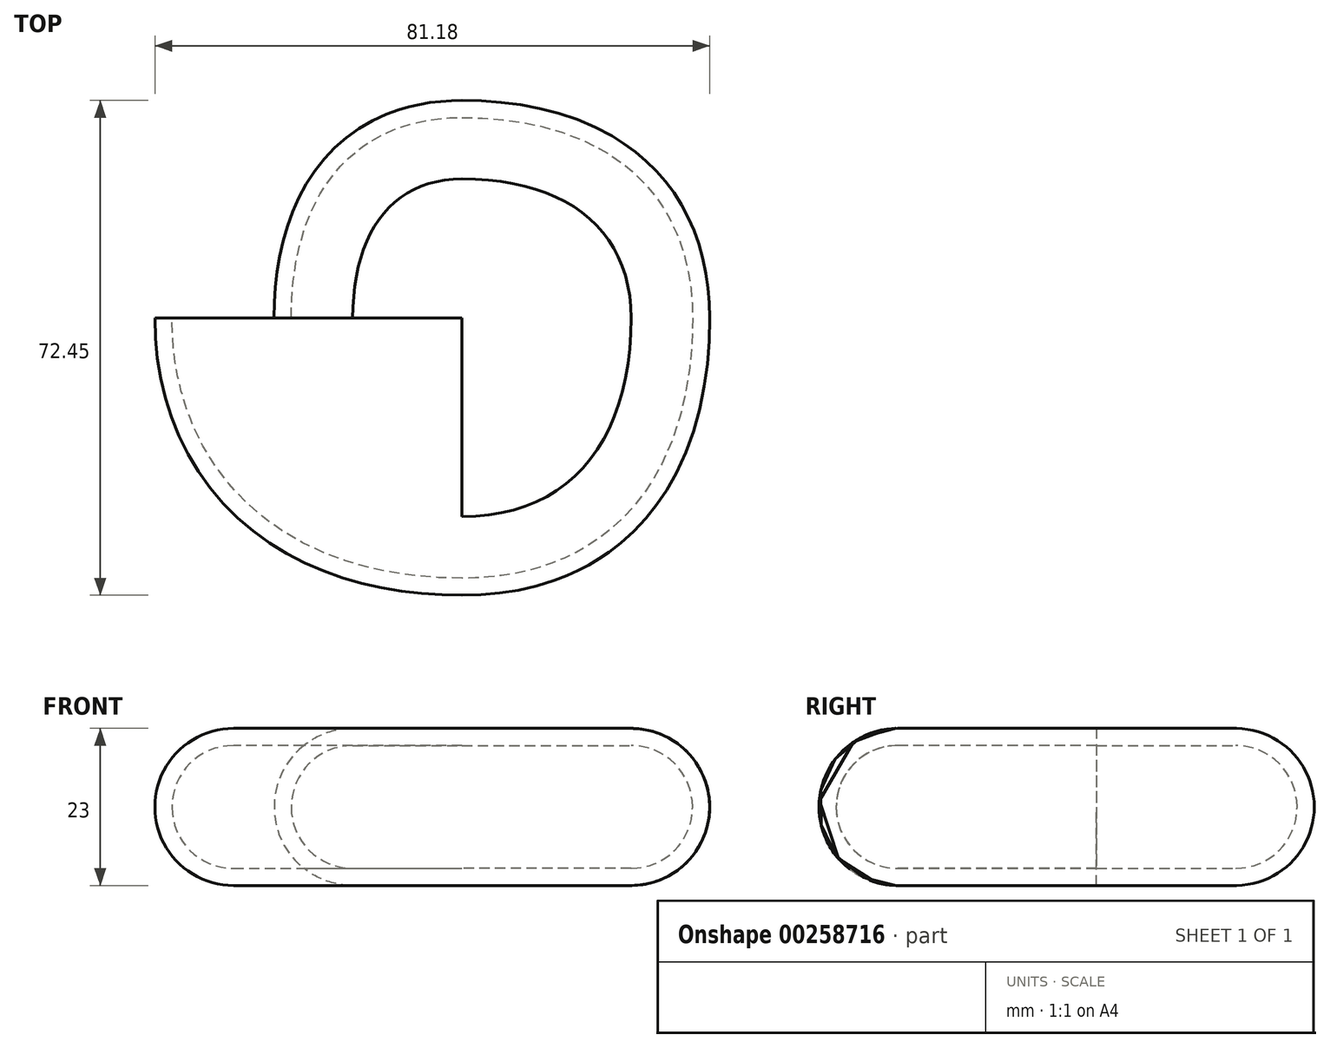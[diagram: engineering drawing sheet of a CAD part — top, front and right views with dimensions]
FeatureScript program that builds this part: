
annotation { "Feature Type Name" : "Feature", "Feature Type Description" : "" }
export const myFeature = defineFeature(function(context is Context, id is Id, definition is map)
    precondition{}
    {
        {
            assignVariable(context, id + "F0", {"name" : "t", "anyValue" : 2.5});
        }
        {
            assignVariable(context, id + "F1", {"name" : "h_base", "anyValue" : 18});
        }
        {
            assignVariable(context, id + "F2", {"name" : "s", "anyValue" : 1.8});
        }
        {
            var Q0;
            Q0=qCreatedBy(makeId("Front.planeOp"),FACE);
            var sketch = newSketch(context, id + "F3", { "sketchPlane" : qUnion([Q0])});
            skLineSegment(sketch, "E0", {"start": v(0, 9) * mm, "end": v(-16, 9) * mm});
            skLineSegment(sketch, "E1", {"start": v(-16, 9) * mm, "end": v(-16, -9) * mm, "construction": true});
            skLineSegment(sketch, "E2", {"start": v(-16, -9) * mm, "end": v(0, -9) * mm});
            skArc(sketch, "E3", {"start": v(-16, 9) * mm, "mid": v(-25, 0) * mm, "end": v(-16, -9) * mm});
            skLineSegment(sketch, "E4", {"start": v(0, 9) * mm, "end": v(0, -9) * mm});
            skPoint(sketch, "E5", {"position": v(-25, 0) * mm});
            skSolve(sketch);
        }
        {
            var Q0;
            Q0=qCreatedBy(makeId("Right.planeOp"),FACE);
            var sketch = newSketch(context, id + "F4", { "sketchPlane" : qUnion([Q0])});
            skLineSegment(sketch, "E6", {"start": v(0, -9) * mm, "end": v(20.36, -9) * mm});
            skLineSegment(sketch, "E7", {"start": v(20.36, -9) * mm, "end": v(20.36, 9) * mm, "construction": true});
            skLineSegment(sketch, "E8", {"start": v(20.36, 9) * mm, "end": v(0, 9) * mm});
            skArc(sketch, "E9", {"start": v(20.36, -9) * mm, "mid": v(29.36, 0) * mm, "end": v(20.36, 9) * mm});
            skLineSegment(sketch, "E10", {"start": v(0, -9) * mm, "end": v(0, 9) * mm});
            skPoint(sketch, "E11", {"position": v(29.36, 0) * mm});
            skSolve(sketch);
        }
        {
            var Q0;
            Q0=qCreatedBy(makeId("Front.planeOp"),FACE);
            var sketch = newSketch(context, id + "F5", { "sketchPlane" : qUnion([Q0])});
            skLineSegment(sketch, "E12", {"start": v(0, -9) * mm, "end": v(24.73, -9) * mm});
            skLineSegment(sketch, "E13", {"start": v(24.73, -9) * mm, "end": v(24.73, 9) * mm, "construction": true});
            skLineSegment(sketch, "E14", {"start": v(24.73, 9) * mm, "end": v(0, 9) * mm});
            skArc(sketch, "E15", {"start": v(24.73, -9) * mm, "mid": v(33.73, 0) * mm, "end": v(24.73, 9) * mm});
            skLineSegment(sketch, "E16", {"start": v(0, -9) * mm, "end": v(0, 9) * mm});
            skPoint(sketch, "E17", {"position": v(33.73, 0) * mm});
            skSolve(sketch);
        }
        {
            var Q0;
            Q0=qCreatedBy(makeId("Right.planeOp"),FACE);
            var sketch = newSketch(context, id + "F6", { "sketchPlane" : qUnion([Q0])});
            skLineSegment(sketch, "E18", {"start": v(0, 9) * mm, "end": v(-29.09, 9) * mm});
            skLineSegment(sketch, "E19", {"start": v(-29.09, 9) * mm, "end": v(-29.09, -9) * mm, "construction": true});
            skLineSegment(sketch, "E20", {"start": v(-29.09, -9) * mm, "end": v(0, -9) * mm});
            skArc(sketch, "E21", {"start": v(-29.09, 9) * mm, "mid": v(-38.09, 0) * mm, "end": v(-29.09, -9) * mm});
            skLineSegment(sketch, "E22", {"start": v(0, 9) * mm, "end": v(0, -9) * mm});
            skPoint(sketch, "E23", {"position": v(-38.09, 0) * mm});
            skSolve(sketch);
        }
        {
            var Q0;
            Q0=qCreatedBy(makeId("Front.planeOp"),FACE);
            var sketch = newSketch(context, id + "F7", { "sketchPlane" : qUnion([Q0])});
            skLineSegment(sketch, "E24", {"start": v(0, 9) * mm, "end": v(-33.45, 9) * mm});
            skLineSegment(sketch, "E25", {"start": v(-33.45, 9) * mm, "end": v(-33.45, -9) * mm, "construction": true});
            skLineSegment(sketch, "E26", {"start": v(-33.45, -9) * mm, "end": v(0, -9) * mm});
            skArc(sketch, "E27", {"start": v(-33.45, 9) * mm, "mid": v(-42.45, 0) * mm, "end": v(-33.45, -9) * mm});
            skLineSegment(sketch, "E28", {"start": v(0, 9) * mm, "end": v(0, -9) * mm});
            skPoint(sketch, "E29", {"position": v(-42.45, 0) * mm});
            skSolve(sketch);
        }
        {
            var Q0;
            Q0 = qSketchRegion(id + "F3", true);
            var Q1;
            Q1 = qSketchRegion(id + "F4", true);
            var Q2;
            Q2=sQuery(id+"F3.wireOp",VERTEX,"E5");
            var Q3;
            Q3=sQuery(id+"F4.wireOp",VERTEX,"E11");
            loft(context, id + "F8", {"startCondition" : LoftEndDerivativeType.NORMAL_TO_PROFILE, "startMagnitude" : getVariable(context, 's'), "endCondition" : LoftEndDerivativeType.NORMAL_TO_PROFILE, "endMagnitude" : getVariable(context, 's'), "sheetProfilesArray" : [{ "sheetProfileEntities" : qUnion([Q0]) }, { "sheetProfileEntities" : qUnion([Q1]) }], "matchConnections" : true, "connections" : [{ "connectionEntities" : qUnion([Q2, Q3]), "connectionEdgeQueries" : qUnion([]), "connectionEdgeParameters" : [] }]});
        }
        {
            var Q1;
            Q1 = qSketchRegion(id + "F4", true);
            var Q2;
            Q2 = qSketchRegion(id + "F5", true);
            var Q3;
            Q3=makeQuery(id+"F8.opLoft","MID_CAP_VERTEX",VERTEX,{"disambiguationData":[OSD([sQuery(id+"F4.wireOp",VERTEX,"E11")])],"capPos":1.0});
            var Q4;
            Q4=sQuery(id+"F5.wireOp",VERTEX,"E17");
            loft(context, id + "F9", {"operationType" : NewBodyOperationType.ADD, "startCondition" : LoftEndDerivativeType.NORMAL_TO_PROFILE, "startMagnitude" : getVariable(context, 's'), "endCondition" : LoftEndDerivativeType.NORMAL_TO_PROFILE, "endMagnitude" : getVariable(context, 's'), "sheetProfilesArray" : [{ "sheetProfileEntities" : qUnion([Q1]) }, { "sheetProfileEntities" : qUnion([Q2]) }], "matchConnections" : true, "connections" : [{ "connectionEntities" : qUnion([Q3, Q4]), "connectionEdgeQueries" : qUnion([]), "connectionEdgeParameters" : [] }]});
        }
        {
            var Q1;
            Q1 = qSketchRegion(id + "F5", true);
            var Q2;
            Q2 = qSketchRegion(id + "F6", true);
            var Q3;
            Q3=makeQuery(id+"F9.opLoft","MID_CAP_VERTEX",VERTEX,{"disambiguationData":[OSD([sQuery(id+"F5.wireOp",VERTEX,"E17")])],"capPos":1.0});
            var Q4;
            Q4=sQuery(id+"F6.wireOp",VERTEX,"E23");
            loft(context, id + "F10", {"operationType" : NewBodyOperationType.ADD, "startCondition" : LoftEndDerivativeType.NORMAL_TO_PROFILE, "startMagnitude" : getVariable(context, 's'), "endCondition" : LoftEndDerivativeType.NORMAL_TO_PROFILE, "endMagnitude" : getVariable(context, 's'), "sheetProfilesArray" : [{ "sheetProfileEntities" : qUnion([Q1]) }, { "sheetProfileEntities" : qUnion([Q2]) }], "matchConnections" : true, "connections" : [{ "connectionEntities" : qUnion([Q3, Q4]), "connectionEdgeQueries" : qUnion([]), "connectionEdgeParameters" : [] }]});
        }
        {
            var Q0;
            Q0=qCreatedBy(makeId("Top.planeOp"),FACE);
            var sketch = newSketch(context, id + "F11", { "sketchPlane" : qUnion([Q0])});
            skFitSpline(sketch, "E30", {"points": [v(0, -38.09) * mm, v(-42.45, 0) * mm], "startDerivative": vector(-82.63, 0) * mm, "endDerivative": vector(0, 63.86) * mm});
            skLineSegment(sketch, "E31", {"start": v(-27.54, -38.09) * mm, "end": v(0, -38.09) * mm, "construction": true});
            skLineSegment(sketch, "E32", {"start": v(-42.45, 0) * mm, "end": v(-42.45, -21.29) * mm, "construction": true});
            skSolve(sketch);
        }
        {
            var Q1;
            Q1 = qSketchRegion(id + "F6", true);
            var Q2;
            Q2 = qSketchRegion(id + "F7", true);
            var Q3;
            Q3=sQuery(id+"F11.wireOp",EDGE,"E30");
            loft(context, id + "F12", {"operationType" : NewBodyOperationType.ADD, "addGuides" : true, "sheetProfilesArray" : [{ "sheetProfileEntities" : qUnion([Q1]) }, { "sheetProfileEntities" : qUnion([Q2]) }], "guidesArray" : [{ "guideEntities" : qUnion([Q3]), "guideDerivativeType" : LoftGuideDerivativeType.DEFAULT, "guideDerivativeMagnitude" : 1 }]});
        }
        {
            var Q0;
            Q0=makeQuery(id+"F12.opLoft","CAP_FACE",FACE,{"disambiguationData":[OSD([makeQuery(id+"F7.imprint","IMPRINT",FACE,{"disambiguationData":[TD([[makeQuery(id+"F7.imprint","IMPRINT",EDGE,{"derivedFrom":sQuery(id+"F7.wireOp",EDGE,"E24")}),1.0]])]})])],"isStart":true});
            shell(context, id + "F13", {"entities" : qUnion([Q0]), "thickness" : (getVariable(context, 't')) * mm, "oppositeDirection" : true});
        }
        {
            var Q0;
            Q0=qCreatedBy(makeId("Front.planeOp"),FACE);
            var sketch = newSketch(context, id + "F14", { "sketchPlane" : qUnion([Q0])});
            skLineSegment(sketch, "E33", {"start": v(0, -33.82) * mm, "end": v(0, 55.33) * mm, "construction": true});
            skSolve(sketch);
        }
        {
            var Q0;
            Q0=qCreatedBy(makeId("Front.planeOp"),FACE);
            var Q1;
            Q1=sQuery(id+"F14.wireOp",EDGE,"E33");
            cPlane(context, id + "F15", {"entities" : qUnion([Q0, Q1]), "cplaneType" : CPlaneType.LINE_ANGLE, "offset" : 25 * mm, "angle" : 45 * degree, "width" : 150 * mm, "height" : 150 * mm});
        }
        {
            var Q0;
            Q0=qCreatedBy(id+"F15.planeOp",FACE);
            cPlane(context, id + "F16", {"entities" : qUnion([Q0]), "cplaneType" : CPlaneType.OFFSET, "offset" : 50 * mm, "width" : 150 * mm, "height" : 150 * mm});
        }
        {
            var Q0;
            Q0=qCreatedBy(id+"F16.planeOp",FACE);
            var sketch = newSketch(context, id + "F17", { "sketchPlane" : qUnion([Q0])});
            skCircle(sketch, "E34", {"center": v(0, 0) * mm, "radius": 9 * mm});
            skPoint(sketch, "E35", {"position": v(0, 9) * mm});
            skPoint(sketch, "E36", {"position": v(9, 0) * mm});
            skPoint(sketch, "E37", {"position": v(-9, 0) * mm});
            skPoint(sketch, "E38", {"position": v(0, -9) * mm});
            skSolve(sketch);
        }
        {
            var Q0;
            Q0=qCreatedBy(makeId("Top.planeOp"),FACE);
            var Q1;
            Q1=sQuery(id+"F17.wireOp",VERTEX,"E35");
            cPlane(context, id + "F18", {"entities" : qUnion([Q0, Q1]), "cplaneType" : CPlaneType.PLANE_POINT, "offset" : (getVariable(context, 'h_base') / 2) * mm, "width" : 150 * mm, "height" : 150 * mm});
        }
        {
            var Q0;
            Q0=qCreatedBy(id+"F18.planeOp",FACE);
            var sketch = newSketch(context, id + "F19", { "sketchPlane" : qUnion([Q0])});
            skFitSpline(sketch, "E39", {"points": [v(-35.36, 35.36) * mm, v(-32.21, 19) * mm, v(-23.16, 0) * mm], "startDerivative": vector(35.76, -30.93) * mm, "endDerivative": vector(0, -36.11) * mm});
            skSolve(sketch);
        }
        {
            var Q0;
            Q0=qCreatedBy(makeId("Top.planeOp"),FACE);
            var Q1;
            Q1=sQuery(id+"F17.wireOp",VERTEX,"E38");
            cPlane(context, id + "F20", {"entities" : qUnion([Q0, Q1]), "cplaneType" : CPlaneType.PLANE_POINT, "offset" : 25 * mm, "width" : 150 * mm, "height" : 150 * mm});
        }
    });
